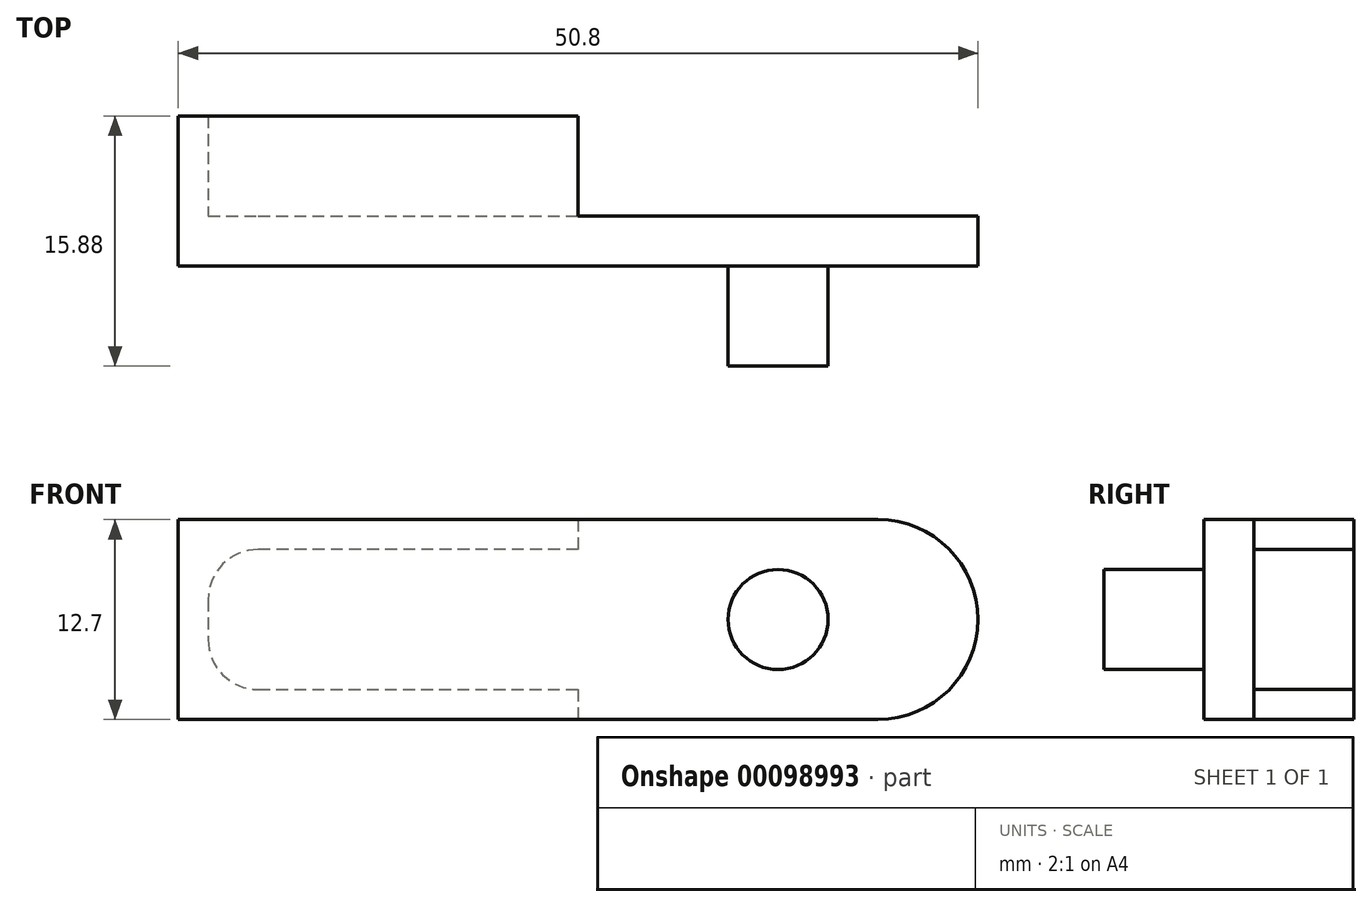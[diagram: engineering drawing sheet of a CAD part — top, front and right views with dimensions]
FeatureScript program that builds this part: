
annotation { "Feature Type Name" : "Feature", "Feature Type Description" : "" }
export const myFeature = defineFeature(function(context is Context, id is Id, definition is map)
    precondition{}
    {
        {
            var Q0;
            Q0=qCreatedBy(makeId("Front.planeOp"),FACE);
            var sketch = newSketch(context, id + "F0", { "sketchPlane" : qUnion([Q0])});
            skLineSegment(sketch, "E0.bottom", {"start": v(0, 0) * mm, "end": v(50.8, 0) * mm});
            skLineSegment(sketch, "E0.top", {"start": v(0, 12.7) * mm, "end": v(50.8, 12.7) * mm});
            skLineSegment(sketch, "E0.left", {"start": v(0, 0) * mm, "end": v(0, 12.7) * mm});
            skLineSegment(sketch, "E0.right", {"start": v(50.8, 0) * mm, "end": v(50.8, 12.7) * mm});
            skSolve(sketch);
        }
        {
            var Q0;
            Q0 = qSketchRegion(id + "F0", true);
            extrude(context, id + "F1", {"entities" : qUnion([Q0]), "depth" : 3.17 * mm});
        }
        {
            var Q0;
            Q0=makeQuery(id+"F1.opExtrude","CAP_FACE",FACE,{"disambiguationData":[OSD([sQuery(id+"F0.wireOp",EDGE,"E0.bottom"),sQuery(id+"F0.wireOp",EDGE,"E0.top"),sQuery(id+"F0.wireOp",EDGE,"E0.left"),sQuery(id+"F0.wireOp",EDGE,"E0.right")])],"isStart":false});
            var sketch = newSketch(context, id + "F2", { "sketchPlane" : qUnion([Q0])});
            skCircle(sketch, "E1", {"center": v(38.1, 6.35) * mm, "radius": 3.18 * mm});
            skPoint(sketch, "E1.centerSnap0", {"position": v(50.8, 6.35) * mm});
            skSolve(sketch);
        }
        {
            var Q0;
            Q0=makeQuery(id+"F2.imprint","IMPRINT",FACE,{"disambiguationData":[TD([[makeQuery(id+"F2.imprint","IMPRINT",EDGE,{"derivedFrom":sQuery(id+"F2.wireOp",EDGE,"E1")}),1.0]])]});
            extrude(context, id + "F3", {"entities" : qUnion([Q0]), "operationType" : NewBodyOperationType.ADD, "depth" : 6.35 * mm});
        }
        {
            var Q0;
            Q0=makeQuery(id+"F1.opExtrude","CAP_FACE",FACE,{"disambiguationData":[OSD([sQuery(id+"F0.wireOp",EDGE,"E0.bottom"),sQuery(id+"F0.wireOp",EDGE,"E0.top"),sQuery(id+"F0.wireOp",EDGE,"E0.left"),sQuery(id+"F0.wireOp",EDGE,"E0.right")])],"isStart":true});
            var sketch = newSketch(context, id + "F4", { "sketchPlane" : qUnion([Q0])});
            skLineSegment(sketch, "E2", {"start": v(0, 12.7) * mm, "end": v(-25.4, 12.7) * mm});
            skLineSegment(sketch, "E3", {"start": v(-25.4, 12.7) * mm, "end": v(-25.4, 10.8) * mm});
            skLineSegment(sketch, "E4", {"start": v(-25.4, 10.8) * mm, "end": v(-1.9, 10.8) * mm});
            skLineSegment(sketch, "E5", {"start": v(-1.9, 10.8) * mm, "end": v(-1.9, 1.9) * mm});
            skLineSegment(sketch, "E6", {"start": v(-1.9, 1.9) * mm, "end": v(-25.4, 1.9) * mm});
            skLineSegment(sketch, "E7", {"start": v(-25.4, 1.9) * mm, "end": v(-25.4, 0) * mm});
            skLineSegment(sketch, "E8", {"start": v(0, 0) * mm, "end": v(0, 12.7) * mm});
            skSolve(sketch);
        }
        {
            var Q0;
            Q0 = qSketchRegion(id + "F4", true);
            var Q1;
            Q1=makeQuery(id+"F4.imprint","IMPRINT",FACE,{"disambiguationData":[TD([[makeQuery(id+"F4.imprint","IMPRINT",EDGE,{"derivedFrom":sQuery(id+"F4.wireOp",EDGE,"E2")}),1.0]])]});
            extrude(context, id + "F5", {"entities" : qUnion([Q0, Q1]), "operationType" : NewBodyOperationType.ADD, "depth" : 6.35 * mm});
        }
        {
            var Q0;
            Q0=makeQuery(id+"F5.opExtrude","SWEPT_EDGE",EDGE,{"disambiguationData":[OSD([sQuery(id+"F4.wireOp",EDGE,"E4"),sQuery(id+"F4.wireOp",EDGE,"E5")])]});
            var Q1;
            Q1=makeQuery(id+"F5.opExtrude","SWEPT_EDGE",EDGE,{"disambiguationData":[OSD([sQuery(id+"F4.wireOp",EDGE,"E5"),sQuery(id+"F4.wireOp",EDGE,"E6")])]});
            fillet(context, id + "F6", {"entities" : qUnion([Q0, Q1]), "radius" : 3.17 * mm, "tangentPropagation" : true, "allowEdgeOverflow" : false});
        }
        {
            var Q0;
            Q0=makeQuery(id+"F1.opExtrude","SWEPT_EDGE",EDGE,{"disambiguationData":[OSD([sQuery(id+"F0.wireOp",EDGE,"E0.top"),sQuery(id+"F0.wireOp",EDGE,"E0.right")])]});
            var Q1;
            Q1=makeQuery(id+"F1.opExtrude","SWEPT_EDGE",EDGE,{"disambiguationData":[OSD([sQuery(id+"F0.wireOp",EDGE,"E0.bottom"),sQuery(id+"F0.wireOp",EDGE,"E0.right")])]});
            fillet(context, id + "F7", {"entities" : qUnion([Q0, Q1]), "radius" : 6.35 * mm, "tangentPropagation" : true, "allowEdgeOverflow" : false});
        }
    });
